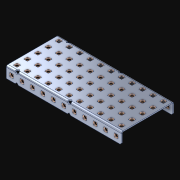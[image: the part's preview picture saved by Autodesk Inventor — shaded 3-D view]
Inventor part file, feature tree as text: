
AUTODESK INVENTOR PART (.ipt)
format: ipt  version: 2021 (Build 250183000, 183)  size: 1,699,840 bytes
history: native  units: in
note: dims shown in document units (in); Inventor stores cm internally (conversion verified against a paired STEP export)
features: extrude x78, other x78, sketch x4, pattern_linear x3
ambient origin geometry x8: Origin, YZ Plane, XZ Plane, XY Plane, X Axis, Y Axis, Z Axis, Center Point
bodies: Solid1 (feature_tree)
feature tree (163):
  pattern_linear  "Rectangular Pattern1"  Spacing1=0.182in  [1 undecoded]
  pattern_linear  "Rectangular Pattern2"  Spacing1=0.046in  [1 undecoded]
  pattern_linear  "Rectangular Pattern3"  Spacing1=0.5in  [1 undecoded]
  extrude  "Extrusion1"  Depth=0.046in
  sketch  "Sketch1"  dims[d0=0.182in]
  other  "Srf1"
  sketch  "Sketch2"  dims[d1=0.046in d2=0.0in]
  other  "Srf2"
  sketch  "Sketch3"  dims[d3=0.182in]
  other  "Srf3"
  other  "Srf4"
  other  "Srf5"
  other  "Srf6"
  other  "Srf7"
  other  "Srf8"
  other  "Srf9"
  other  "Srf10"
  other  "Srf11"
  other  "Srf12"
  other  "Srf13"
  other  "Srf38"
  other  "Srf39"
  other  "Srf40"
  other  "Srf41"
  other  "Srf42"
  other  "Srf43"
  other  "Srf44"
  other  "Srf45"
  other  "Srf46"
  other  "Srf47"
  other  "Srf72"
  other  "Srf73"
  other  "Srf74"
  other  "Srf75"
  other  "Srf76"
  other  "Srf77"
  other  "Srf78"
  other  "Srf79"
  other  "Srf80"
  other  "Srf81"
  other  "Srf82"
  other  "Srf107"
  other  "Srf108"
  other  "Srf109"
  other  "Srf110"
  other  "Srf111"
  other  "Srf112"
  other  "Srf113"
  other  "Srf114"
  other  "Srf115"
  other  "Srf116"
  other  "Srf117"
  other  "Srf142"
  other  "Srf143"
  other  "Srf144"
  other  "Srf145"
  other  "Srf146"
  other  "Srf147"
  other  "Srf148"
  other  "Srf149"
  other  "Srf150"
  other  "Srf151"
  other  "Srf152"
  other  "Srf177"
  other  "Srf178"
  other  "Srf179"
  other  "Srf180"
  other  "Srf181"
  other  "Srf182"
  other  "Srf183"
  other  "Srf184"
  other  "Srf185"
  other  "Srf186"
  other  "Srf187"
  other  "Srf212"
  other  "Srf213"
  other  "Srf214"
  other  "Srf215"
  other  "Srf216"
  other  "Srf217"
  other  "Srf218"
  other  "Srf219"
  other  "Srf220"
  other  "Srf221"
  sketch  "Sketch4"  dims[d4=0.046in d5=0.0in d6=0.182in d7=0.046in d8=0.0in d11=0.5in d12=4.3307in d14=0.5in d15=1.9685in d17=0.5in d18=4.3307in d20=0.5in d21=12.0in d22=0.0in]
  parser-record x1  (decoder bookkeeping rows leaked as tree rows — omitted from the tree; the rows remain in map.json)
  extrude  "ExtrusionSrf1"  Depth=0.046in
  extrude  "ExtrusionSrf2"  Depth=0.046in
  extrude  "ExtrusionSrf3"  Depth=0.046in
  extrude  "ExtrusionSrf4"  Depth=0.046in
  extrude  "ExtrusionSrf5"  Depth=0.046in
  extrude  "ExtrusionSrf6"  TaperAngle=0.0deg  [1 undecoded]
  extrude  "ExtrusionSrf7"  [1 undecoded]
  extrude  "ExtrusionSrf8"  [1 undecoded]
  extrude  "ExtrusionSrf9"  [1 undecoded]
  extrude  "ExtrusionSrf10"  [1 undecoded]
  extrude  "ExtrusionSrf11"  [1 undecoded]
  extrude  "ExtrusionSrf12"  [1 undecoded]
  extrude  "ExtrusionSrf13"  [1 undecoded]
  extrude  "ExtrusionSrf38"  [1 undecoded]
  extrude  "ExtrusionSrf39"  [1 undecoded]
  extrude  "ExtrusionSrf40"  [1 undecoded]
  extrude  "ExtrusionSrf41"  [1 undecoded]
  extrude  "ExtrusionSrf42"  [1 undecoded]
  extrude  "ExtrusionSrf43"  [1 undecoded]
  extrude  "ExtrusionSrf44"  [1 undecoded]
  extrude  "ExtrusionSrf45"  [1 undecoded]
  extrude  "ExtrusionSrf46"  [1 undecoded]
  extrude  "ExtrusionSrf47"  [1 undecoded]
  extrude  "ExtrusionSrf72"  [1 undecoded]
  extrude  "ExtrusionSrf73"  [1 undecoded]
  extrude  "ExtrusionSrf74"  [1 undecoded]
  extrude  "ExtrusionSrf75"  [1 undecoded]
  extrude  "ExtrusionSrf76"  [1 undecoded]
  extrude  "ExtrusionSrf77"  [1 undecoded]
  extrude  "ExtrusionSrf78"  [1 undecoded]
  extrude  "ExtrusionSrf79"  [1 undecoded]
  extrude  "ExtrusionSrf80"  [1 undecoded]
  extrude  "ExtrusionSrf81"  [1 undecoded]
  extrude  "ExtrusionSrf82"  [1 undecoded]
  extrude  "ExtrusionSrf107"  [1 undecoded]
  extrude  "ExtrusionSrf108"  [1 undecoded]
  extrude  "ExtrusionSrf109"  [1 undecoded]
  extrude  "ExtrusionSrf110"  [1 undecoded]
  extrude  "ExtrusionSrf111"  [1 undecoded]
  extrude  "ExtrusionSrf112"  [1 undecoded]
  extrude  "ExtrusionSrf113"  [1 undecoded]
  extrude  "ExtrusionSrf114"  [1 undecoded]
  extrude  "ExtrusionSrf115"  [1 undecoded]
  extrude  "ExtrusionSrf116"  [1 undecoded]
  extrude  "ExtrusionSrf117"  [1 undecoded]
  extrude  "ExtrusionSrf142"  [1 undecoded]
  extrude  "ExtrusionSrf143"  [1 undecoded]
  extrude  "ExtrusionSrf144"  [1 undecoded]
  extrude  "ExtrusionSrf145"  [1 undecoded]
  extrude  "ExtrusionSrf146"  [1 undecoded]
  extrude  "ExtrusionSrf147"  [1 undecoded]
  extrude  "ExtrusionSrf148"  [1 undecoded]
  extrude  "ExtrusionSrf149"  [1 undecoded]
  extrude  "ExtrusionSrf150"  [1 undecoded]
  extrude  "ExtrusionSrf151"  [1 undecoded]
  extrude  "ExtrusionSrf152"  [1 undecoded]
  extrude  "ExtrusionSrf177"  [1 undecoded]
  extrude  "ExtrusionSrf178"  [1 undecoded]
  extrude  "ExtrusionSrf179"  [1 undecoded]
  extrude  "ExtrusionSrf180"  [1 undecoded]
  extrude  "ExtrusionSrf181"  [1 undecoded]
  extrude  "ExtrusionSrf182"  [1 undecoded]
  extrude  "ExtrusionSrf183"  [1 undecoded]
  extrude  "ExtrusionSrf184"  [1 undecoded]
  extrude  "ExtrusionSrf185"  [1 undecoded]
  extrude  "ExtrusionSrf186"  [1 undecoded]
  extrude  "ExtrusionSrf187"  [1 undecoded]
  extrude  "ExtrusionSrf212"  [1 undecoded]
  extrude  "ExtrusionSrf213"  [1 undecoded]
  extrude  "ExtrusionSrf214"  [1 undecoded]
  extrude  "ExtrusionSrf215"  [1 undecoded]
  extrude  "ExtrusionSrf216"  [1 undecoded]
  extrude  "ExtrusionSrf217"  [1 undecoded]
  extrude  "ExtrusionSrf218"  [1 undecoded]
  extrude  "ExtrusionSrf219"  [1 undecoded]
  extrude  "ExtrusionSrf220"  [1 undecoded]
  extrude  "ExtrusionSrf221"  [1 undecoded]
note: 75 required parameter values undecoded (feature->parameter linkage not recoverable at this tier; creation-order binding heuristic only, values carry confidence <= 0.55)
